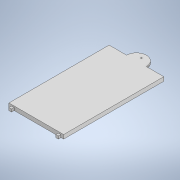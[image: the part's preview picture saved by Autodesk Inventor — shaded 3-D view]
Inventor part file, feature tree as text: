
AUTODESK INVENTOR PART (.ipt)
format: ipt  version: 2020 (Build 240168000, 168)  size: 167,424 bytes
history: native  units: mm
features: sketch x5, extrude x4, hole x1, fillet x1
ambient origin geometry x8: Origin, YZ Plane, XZ Plane, XY Plane, X Axis, Y Axis, Z Axis, Center Point
bodies: Solid1 (feature_tree)
feature tree (11):
  extrude  "Extrusion1"  Depth=76.0mm
  extrude  "Extrusion2"  Depth=2.0mm
  extrude  "Extrusion3"  Depth=2.0mm
  hole  "Hole1"  [1 undecoded]
  extrude  "Extrusion4"  Depth=2.0mm TaperAngle=0.0deg
  fillet  "Fillet1"  Radius=15.0mm
  sketch  "Sketch1"  dims[d0=41.5mm d1=76.0mm]
  sketch  "Sketch2"  dims[d2=3.0mm d3=0.0mm d4=2.0mm]
  sketch  "Sketch3"  dims[d5=2.0mm d6=2.0mm]
  sketch  "Sketch4"  dims[d7=2.0mm d8=2.0mm]
  sketch  "Sketch5"  dims[d9=2.0mm d10=2.0mm d11=0.0mm d12=15.0mm d13=1.5mm d14=0.0mm d15=3.75mm d16=1.0mm d17=6.0mm d18=4.0mm d19=2.0mm d20=90.0deg d21=2.0mm d22=20.594885mm d23=3.0mm d24=3.0mm d25=17.0mm d26=0.5mm d27=0.0mm d28=2.5mm]
note: 1 required parameter value undecoded (feature->parameter linkage not recoverable at this tier; creation-order binding heuristic only, values carry confidence <= 0.55)
